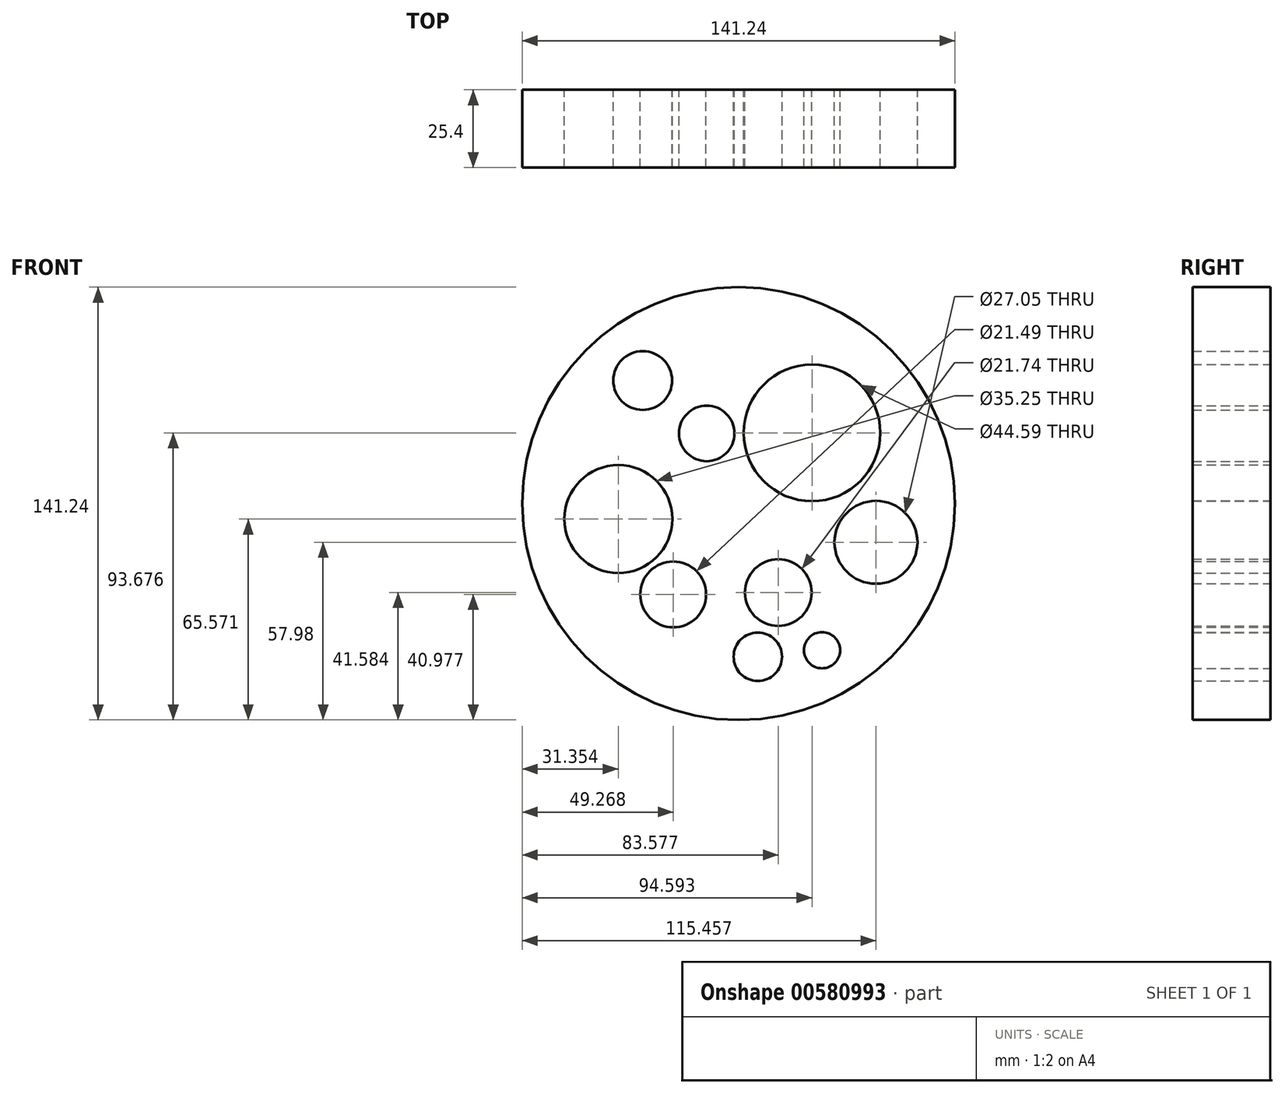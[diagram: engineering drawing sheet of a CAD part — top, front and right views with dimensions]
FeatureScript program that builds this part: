
annotation { "Feature Type Name" : "Feature", "Feature Type Description" : "" }
export const myFeature = defineFeature(function(context is Context, id is Id, definition is map)
    precondition{}
    {
        {
            var Q0;
            Q0=qCreatedBy(makeId("Front.planeOp"),FACE);
            var sketch = newSketch(context, id + "F0", { "sketchPlane" : qUnion([Q0])});
            skCircle(sketch, "E0", {"center": v(0, 0) * mm, "radius": 70.62 * mm});
            skFitSpline(sketch, "E1", {"points": [v(-36.5, 54.2) * mm, v(-10.23, 65.5) * mm, v(-9.92, 65.5) * mm, v(16.34, 62.76) * mm, v(17.25, 62.76) * mm, v(43.21, 45.96) * mm, v(59.7, 23.06) * mm, v(60.62, -18.78) * mm, v(9, -63.67) * mm, v(-46.88, -38.94) * mm, v(-47.18, -38.94) * mm, v(-63.06, 0) * mm, v(-36.5, 54.2) * mm]});
            skCircle(sketch, "E2", {"center": v(-31.3, 40.16) * mm, "radius": 9.59 * mm});
            skCircle(sketch, "E3", {"center": v(23.97, 23.06) * mm, "radius": 22.3 * mm});
            skCircle(sketch, "E4", {"center": v(-39.27, -5.05) * mm, "radius": 17.63 * mm});
            skCircle(sketch, "E5", {"center": v(12.96, -29.04) * mm, "radius": 10.87 * mm});
            skCircle(sketch, "E6", {"center": v(-21.35, -29.64) * mm, "radius": 10.74 * mm});
            skCircle(sketch, "E7", {"center": v(-10.42, 22.88) * mm, "radius": 9.06 * mm});
            skCircle(sketch, "E8", {"center": v(44.84, -12.64) * mm, "radius": 13.53 * mm});
            skCircle(sketch, "E9", {"center": v(27.23, -47.86) * mm, "radius": 5.9 * mm});
            skCircle(sketch, "E10", {"center": v(6.28, -49.99) * mm, "radius": 7.9 * mm});
            skSolve(sketch);
        }
        {
            var Q0;
            Q0 = qSketchRegion(id + "F0", true);
            var Q1;
            Q1=makeQuery(id+"F0.imprint","IMPRINT",FACE,{"disambiguationData":[TD([[makeQuery(id+"F0.imprint","IMPRINT",EDGE,{"derivedFrom":sQuery(id+"F0.wireOp",EDGE,"E1")}),-1.0]])]});
            extrude(context, id + "F1", {"entities" : qUnion([Q0, Q1]), "depth" : 25.4 * mm, "offsetDistance" : 25.4 * mm});
        }
    });
